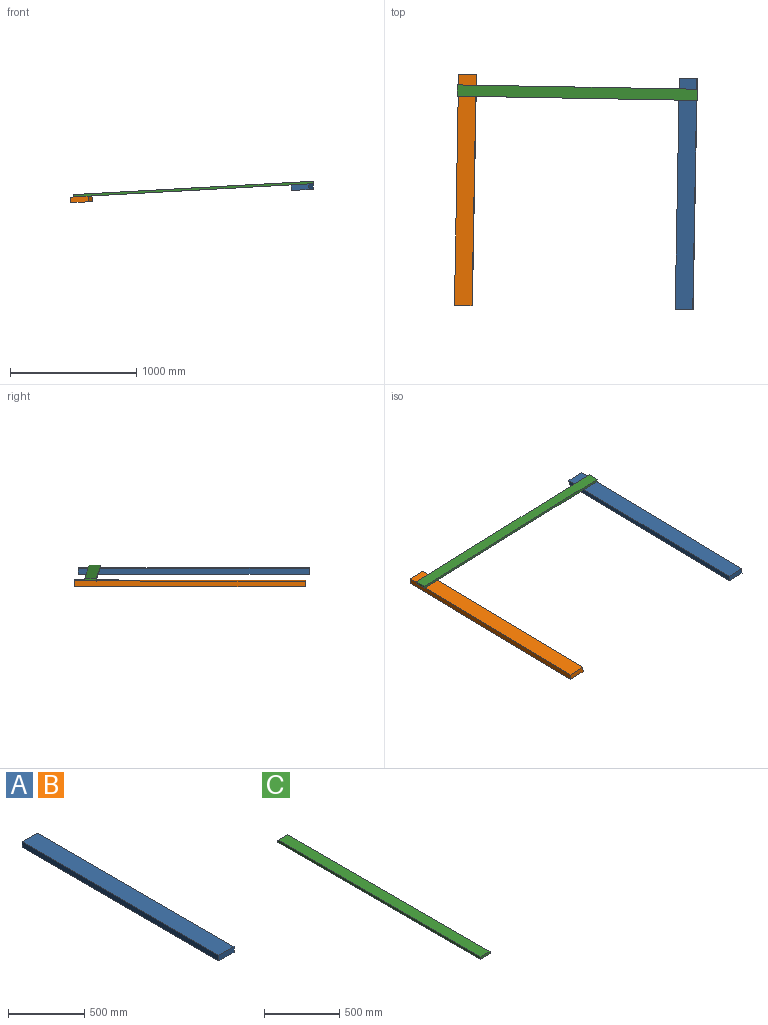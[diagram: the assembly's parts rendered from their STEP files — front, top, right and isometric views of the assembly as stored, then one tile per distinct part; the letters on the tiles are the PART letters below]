
ASSEMBLY  parts=3 mates=2
PART A: 6 faces, bbox 139.7x1828.8x44.5 mm
  f0: plane 1828.8x139.7mm, normal (0,0,-1), area 255483.4mm2, adj f1,f3,f4,f5
  f1: plane 1828.8x44.45mm, normal (1,0,0), area 81290.2mm2, adj f0,f2,f4,f5
  f2: plane 1828.8x139.7mm, normal (0,0,1), area 255483.4mm2, adj f1,f3,f4,f5
  f3: plane 1828.8x44.45mm, normal (-1,0,0), area 81290.2mm2, adj f0,f2,f4,f5
  f4: plane 139.7x44.45mm, normal (0,-1,0), area 6209.7mm2, adj f0,f1,f2,f3
  f5: plane 139.7x44.45mm, normal (0,1,0), area 6209.7mm2, adj f0,f1,f2,f3
PART B: same geometry as A
PART C: 6 faces, bbox 88.9x1905x19.1 mm
  f0: plane 1905x88.9mm, normal (0,0,-1), area 169354.5mm2, adj f1,f3,f4,f5
  f1: plane 1905x19.05mm, normal (1,0,0), area 36290.2mm2, adj f0,f2,f4,f5
  f2: plane 1905x88.9mm, normal (0,0,1), area 169354.5mm2, adj f1,f3,f4,f5
  f3: plane 1905x19.05mm, normal (-1,0,0), area 36290.2mm2, adj f0,f2,f4,f5
  f4: plane 88.9x19.05mm, normal (0,-1,0), area 1693.5mm2, adj f0,f1,f2,f3
  f5: plane 88.9x19.05mm, normal (0,1,0), area 1693.5mm2, adj f0,f1,f2,f3
PLACE A rot(axis=(0.01,-0.95,-0.31),3.3deg) t=(1989.72,-45.07,1526.91)mm
PLACE B rot(axis=(0.01,-0.95,-0.31),3.3deg) t=(240.11,-13.56,1429.54)mm
PLACE C rot(axis=(0.03,-0.03,-1),91.1deg) t=(2061.74,-173.42,1562.72)mm
MATE fastened B.f2 <-> C.f0  axis (-0.06,0,1) through (236.59,-140.54,1451.6)mm
MATE fastened A.f2 <-> C.f0  axis (-0.06,0,1) through (1986.2,-172.05,1548.98)mm
